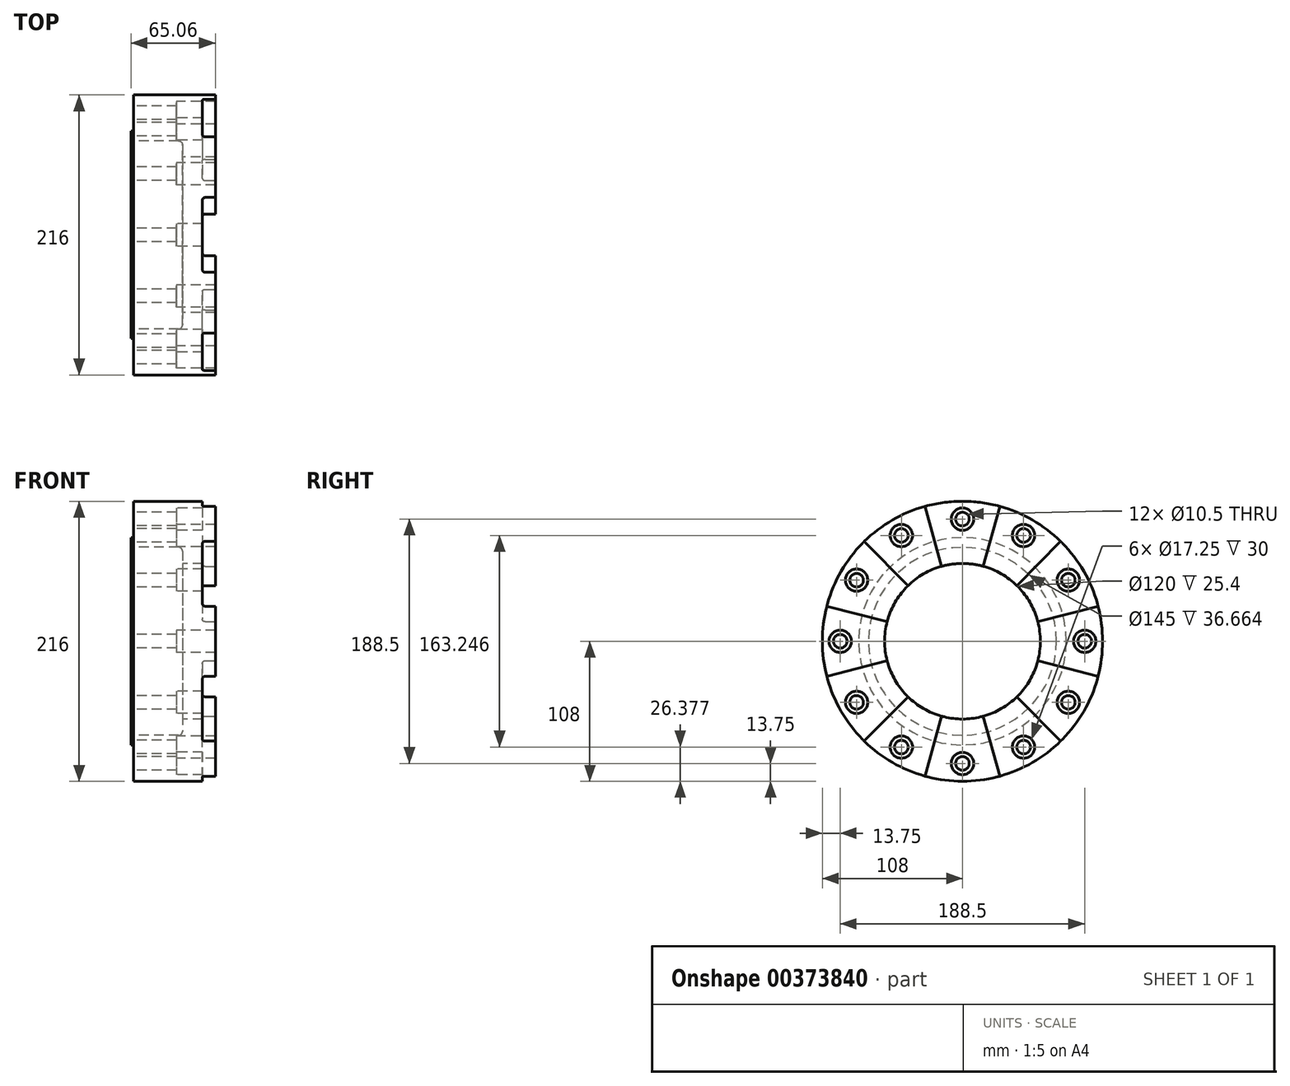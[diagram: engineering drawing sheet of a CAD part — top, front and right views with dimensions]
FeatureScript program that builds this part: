
annotation { "Feature Type Name" : "Feature", "Feature Type Description" : "" }
export const myFeature = defineFeature(function(context is Context, id is Id, definition is map)
    precondition{}
    {
        {
            var Q0;
            Q0=qCreatedBy(makeId("Front.planeOp"),FACE);
            var sketch = newSketch(context, id + "F0", { "sketchPlane" : qUnion([Q0])});
            skLineSegment(sketch, "E0", {"start": v(0, 0) * mm, "end": v(87.54, 0) * mm, "construction": true});
            skLineSegment(sketch, "E1", {"start": v(79.56, 108) * mm, "end": v(79.56, 60) * mm});
            skLineSegment(sketch, "E2", {"start": v(79.56, 60) * mm, "end": v(54.16, 60) * mm});
            skLineSegment(sketch, "E3", {"start": v(54.16, 60) * mm, "end": v(54.16, 69.5) * mm});
            skPoint(sketch, "E4.visualSharp", {"position": v(54.16, 72.5) * mm});
            skLineSegment(sketch, "E5", {"start": v(16.5, 80) * mm, "end": v(16.5, 108) * mm});
            skLineSegment(sketch, "E6", {"start": v(16.5, 108) * mm, "end": v(79.56, 108) * mm});
            skLineSegment(sketch, "E7", {"start": v(14.5, 72.5) * mm, "end": v(14.5, 80) * mm});
            skLineSegment(sketch, "E8", {"start": v(14.5, 80) * mm, "end": v(16.5, 80) * mm});
            skLineSegment(sketch, "E9", {"start": v(14.5, 72.5) * mm, "end": v(51.16, 72.5) * mm});
            skArc(sketch, "E10.filletArc", {"start": v(54.16, 69.5) * mm, "mid": v(53.29, 71.62) * mm, "end": v(51.16, 72.5) * mm});
            skSolve(sketch);
        }
        {
            var Q0;
            Q0=qSketchRegion(id+"F0",true);
            var Q1;
            Q1=sQuery(id+"F0.wireOp",EDGE,"E0");
            revolve(context, id + "F1", {"entities" : qUnion([Q0]), "axis" : qUnion([Q1]), "revolveType" : RevolveType.FULL});
        }
        {
            var Q0;
            Q0=makeQuery(id+"F1.opRevolve","SWEPT_FACE",FACE,{"disambiguationData":[OSD([sQuery(id+"F0.wireOp",EDGE,"E1")])]});
            var sketch = newSketch(context, id + "F2", { "sketchPlane" : qUnion([Q0])});
            skLineSegment(sketch, "E11", {"start": v(0, 0) * mm, "end": v(0, 110.4) * mm, "construction": true});
            skArc(sketch, "E12", {"start": v(-16.03, 57.82) * mm, "mid": v(0, 60) * mm, "end": v(16.03, 57.82) * mm});
            skArc(sketch, "E13", {"start": v(-28.86, 104.07) * mm, "mid": v(0, 108) * mm, "end": v(28.86, 104.07) * mm});
            skLineSegment(sketch, "E14", {"start": v(-28.86, 104.07) * mm, "end": v(-16.03, 57.82) * mm});
            skLineSegment(sketch, "E15", {"start": v(28.86, 104.07) * mm, "end": v(16.03, 57.82) * mm});
            skLineSegment(sketch, "E16.1.0", {"start": v(-75.7, 77.03) * mm, "end": v(-42.05, 42.8) * mm});
            skArc(sketch, "E16.1.1", {"start": v(-58.09, 15.02) * mm, "mid": v(-51.96, 30) * mm, "end": v(-42.05, 42.8) * mm});
            skArc(sketch, "E16.1.2", {"start": v(-104.56, 27.04) * mm, "mid": v(-93.53, 54) * mm, "end": v(-75.7, 77.03) * mm});
            skLineSegment(sketch, "E16.1.3", {"start": v(-104.56, 27.04) * mm, "end": v(-58.09, 15.02) * mm});
            skLineSegment(sketch, "E16.2.0", {"start": v(-104.56, -27.04) * mm, "end": v(-58.09, -15.02) * mm});
            skArc(sketch, "E16.2.1", {"start": v(-42.05, -42.8) * mm, "mid": v(-51.96, -30) * mm, "end": v(-58.09, -15.02) * mm});
            skArc(sketch, "E16.2.2", {"start": v(-75.7, -77.03) * mm, "mid": v(-93.53, -54) * mm, "end": v(-104.56, -27.04) * mm});
            skLineSegment(sketch, "E16.2.3", {"start": v(-75.7, -77.03) * mm, "end": v(-42.05, -42.8) * mm});
            skLineSegment(sketch, "E16.3.0", {"start": v(-28.86, -104.07) * mm, "end": v(-16.03, -57.82) * mm});
            skArc(sketch, "E16.3.1", {"start": v(16.03, -57.82) * mm, "mid": v(0, -60) * mm, "end": v(-16.03, -57.82) * mm});
            skArc(sketch, "E16.3.2", {"start": v(28.86, -104.07) * mm, "mid": v(0, -108) * mm, "end": v(-28.86, -104.07) * mm});
            skLineSegment(sketch, "E16.3.3", {"start": v(28.86, -104.07) * mm, "end": v(16.03, -57.82) * mm});
            skLineSegment(sketch, "E16.4.0", {"start": v(75.7, -77.03) * mm, "end": v(42.05, -42.8) * mm});
            skArc(sketch, "E16.4.1", {"start": v(58.09, -15.02) * mm, "mid": v(51.96, -30) * mm, "end": v(42.05, -42.8) * mm});
            skArc(sketch, "E16.4.2", {"start": v(104.56, -27.04) * mm, "mid": v(93.53, -54) * mm, "end": v(75.7, -77.03) * mm});
            skLineSegment(sketch, "E16.4.3", {"start": v(104.56, -27.04) * mm, "end": v(58.09, -15.02) * mm});
            skLineSegment(sketch, "E16.5.0", {"start": v(104.56, 27.04) * mm, "end": v(58.09, 15.02) * mm});
            skArc(sketch, "E16.5.1", {"start": v(42.05, 42.8) * mm, "mid": v(51.96, 30) * mm, "end": v(58.09, 15.02) * mm});
            skArc(sketch, "E16.5.2", {"start": v(75.7, 77.03) * mm, "mid": v(93.53, 54) * mm, "end": v(104.56, 27.04) * mm});
            skLineSegment(sketch, "E16.5.3", {"start": v(75.7, 77.03) * mm, "end": v(42.05, 42.8) * mm});
            skSolve(sketch);
        }
        {
            var Q0;
            Q0=qSketchRegion(id+"F2",true);
            extrude(context, id + "F3", {"entities" : qUnion([Q0]), "operationType" : NewBodyOperationType.REMOVE, "oppositeDirection" : true, "depth" : 10 * mm});
        }
        {
            var Q0;
            Q0=makeQuery(id+"F3.boolean.opBoolean","SPLIT",FACE,{"disambiguationData":[TD([makeQuery(id+"F3.opExtrude","SWEPT_FACE",FACE,{"disambiguationData":[OSD([sQuery(id+"F2.wireOp",EDGE,"E14")])]})])],"derivedFrom":makeQuery(id+"F1.opRevolve","SWEPT_FACE",FACE,{"disambiguationData":[OSD([sQuery(id+"F0.wireOp",EDGE,"E1")])]})});
            var sketch = newSketch(context, id + "F4", { "sketchPlane" : qUnion([Q0])});
            skLineSegment(sketch, "E17", {"start": v(0, 0) * mm, "end": v(0, 94.25) * mm, "construction": true});
            skCircle(sketch, "E18", {"center": v(0, 94.25) * mm, "radius": 5 * mm});
            skCircle(sketch, "E19.1.0", {"center": v(-47.12, 81.62) * mm, "radius": 5 * mm});
            skCircle(sketch, "E19.2.0", {"center": v(-81.62, 47.13) * mm, "radius": 5 * mm});
            skCircle(sketch, "E19.3.0", {"center": v(-94.25, 0) * mm, "radius": 5 * mm});
            skCircle(sketch, "E19.4.0", {"center": v(-81.62, -47.12) * mm, "radius": 5 * mm});
            skCircle(sketch, "E19.5.0", {"center": v(-47.13, -81.62) * mm, "radius": 5 * mm});
            skCircle(sketch, "E19.6.0", {"center": v(0, -94.25) * mm, "radius": 5 * mm});
            skCircle(sketch, "E19.7.0", {"center": v(47.12, -81.62) * mm, "radius": 5 * mm});
            skCircle(sketch, "E19.8.0", {"center": v(81.62, -47.13) * mm, "radius": 5 * mm});
            skCircle(sketch, "E19.9.0", {"center": v(94.25, 0) * mm, "radius": 5 * mm});
            skCircle(sketch, "E19.10.0", {"center": v(81.62, 47.12) * mm, "radius": 5 * mm});
            skCircle(sketch, "E19.11.0", {"center": v(47.12, 81.62) * mm, "radius": 5 * mm});
            skPoint(sketch, "E19.center", {"position": v(0, 0) * mm});
            skCircle(sketch, "E20", {"center": v(0, 0) * mm, "radius": 94.25 * mm, "construction": true});
            skSolve(sketch);
        }
        {
            var Q0;
            Q0=sQuery(id+"F4.wireOp",VERTEX,"E19.1.0.center");
            var Q1;
            Q1=sQuery(id+"F4.wireOp",VERTEX,"E19.3.0.center");
            var Q2;
            Q2=sQuery(id+"F4.wireOp",VERTEX,"E19.5.0.center");
            var Q3;
            Q3=sQuery(id+"F4.wireOp",VERTEX,"E19.11.0.center");
            var Q4;
            Q4=sQuery(id+"F4.wireOp",VERTEX,"E19.9.0.center");
            var Q5;
            Q5=sQuery(id+"F4.wireOp",VERTEX,"E19.7.0.center");
            var Q6;
            Q6=makeQuery(id+"F1.opRevolve","SWEPT_BODY",BODY,{"disambiguationData":[OSD([sQuery(id+"F0.wireOp",EDGE,"cKsjdh96-D89g-5p2D-h3XL-UVhXMyCSQNq4"),sQuery(id+"F0.wireOp",EDGE,"apuWihD5-RSD5-dsa5-vE7C-J3piarLAXm6q"),sQuery(id+"F0.wireOp",EDGE,"KV8aVnY1-u6Om-Dk3w-krVR-1GxTJCxTkb02"),sQuery(id+"F0.wireOp",EDGE,"Kmc8ooil-dtvY-6vtC-WxYi-Np3pAdkpifhF"),sQuery(id+"F0.wireOp",EDGE,"9beadaba-26b4-418a-b517-611681b9f9d4.filletArc"),sQuery(id+"F0.wireOp",EDGE,"E1"),sQuery(id+"F0.wireOp",EDGE,"E2"),sQuery(id+"F0.wireOp",EDGE,"E3"),sQuery(id+"F0.wireOp",EDGE,"DEHAbUA3-ssQc-y9Ke-qyxT-0Mpok7RH61FX"),sQuery(id+"F0.wireOp",EDGE,"E4.filletArc")])]});
            hole(context, id + "F5", {"style" : HoleStyle.C_BORE, "endStyle" : HoleEndStyle.THROUGH, "holeDiameter" : 10.5 * mm, "cBoreDiameter" : 17.25 * mm, "cBoreDepth" : 30 * mm, "majorDiameter" : 5 * mm, "tappedDepth" : 12 * mm, "tapClearance" : 3, "locations" : qUnion([Q0, Q1, Q2, Q3, Q4, Q5]), "scope" : qUnion([Q6]), "startStyle" : HoleStartStyle.SKETCH});
        }
        {
            var Q0;
            Q0=makeQuery(id+"F3.boolean.opBoolean","COPY",FACE,{"derivedFrom":makeQuery(id+"F3.opExtrude","CAP_FACE",FACE,{"disambiguationData":[OSD([sQuery(id+"F2.wireOp",EDGE,"E12"),sQuery(id+"F2.wireOp",EDGE,"E13"),sQuery(id+"F2.wireOp",EDGE,"E14"),sQuery(id+"F2.wireOp",EDGE,"E15")])],"isStart":false})});
            var sketch = newSketch(context, id + "F6", { "sketchPlane" : qUnion([Q0])});
            skPoint(sketch, "E21", {"position": v(0, 94.25) * mm});
            skPoint(sketch, "E22.1.0", {"position": v(-81.62, 47.12) * mm});
            skPoint(sketch, "E22.2.0", {"position": v(-81.62, -47.12) * mm});
            skPoint(sketch, "E22.3.0", {"position": v(0, -94.25) * mm});
            skPoint(sketch, "E22.4.0", {"position": v(81.62, -47.13) * mm});
            skPoint(sketch, "E22.5.0", {"position": v(81.62, 47.12) * mm});
            skPoint(sketch, "E22.center", {"position": v(0, 0) * mm});
            skSolve(sketch);
        }
        {
            var Q0;
            Q0=sQuery(id+"F6.wireOp",VERTEX,"E21");
            var Q1;
            Q1=sQuery(id+"F6.wireOp",VERTEX,"E22.1.0");
            var Q2;
            Q2=sQuery(id+"F6.wireOp",VERTEX,"E22.2.0");
            var Q3;
            Q3=sQuery(id+"F6.wireOp",VERTEX,"E22.3.0");
            var Q4;
            Q4=sQuery(id+"F6.wireOp",VERTEX,"E22.4.0");
            var Q5;
            Q5=sQuery(id+"F6.wireOp",VERTEX,"E22.5.0");
            var Q6;
            Q6=makeQuery(id+"F1.opRevolve","SWEPT_BODY",BODY,{"disambiguationData":[OSD([sQuery(id+"F0.wireOp",EDGE,"cKsjdh96-D89g-5p2D-h3XL-UVhXMyCSQNq4"),sQuery(id+"F0.wireOp",EDGE,"apuWihD5-RSD5-dsa5-vE7C-J3piarLAXm6q"),sQuery(id+"F0.wireOp",EDGE,"KV8aVnY1-u6Om-Dk3w-krVR-1GxTJCxTkb02"),sQuery(id+"F0.wireOp",EDGE,"Kmc8ooil-dtvY-6vtC-WxYi-Np3pAdkpifhF"),sQuery(id+"F0.wireOp",EDGE,"9beadaba-26b4-418a-b517-611681b9f9d4.filletArc"),sQuery(id+"F0.wireOp",EDGE,"E1"),sQuery(id+"F0.wireOp",EDGE,"E2"),sQuery(id+"F0.wireOp",EDGE,"E3"),sQuery(id+"F0.wireOp",EDGE,"DEHAbUA3-ssQc-y9Ke-qyxT-0Mpok7RH61FX"),sQuery(id+"F0.wireOp",EDGE,"E4.filletArc")])]});
            hole(context, id + "F7", {"style" : HoleStyle.C_BORE, "endStyle" : HoleEndStyle.THROUGH, "holeDiameter" : 10.5 * mm, "cBoreDiameter" : 17.25 * mm, "cBoreDepth" : 20 * mm, "majorDiameter" : 5 * mm, "tappedDepth" : 12 * mm, "tapClearance" : 3, "locations" : qUnion([Q0, Q1, Q2, Q3, Q4, Q5]), "scope" : qUnion([Q6]), "startStyle" : HoleStartStyle.SKETCH});
        }
        {
            var Q0;
            Q0=makeQuery(id+"F3.boolean.opBoolean","COPY",EDGE,{"derivedFrom":makeQuery(id+"F3.opExtrude","CAP_EDGE",EDGE,{"disambiguationData":[OSD([sQuery(id+"F2.wireOp",EDGE,"E15")])],"isStart":true})});
            var Q1;
            Q1=makeQuery(id+"F3.boolean.opBoolean","COPY",EDGE,{"derivedFrom":makeQuery(id+"F3.opExtrude","CAP_EDGE",EDGE,{"disambiguationData":[OSD([sQuery(id+"F2.wireOp",EDGE,"E15")])],"isStart":false})});
            var Q2;
            Q2=makeQuery(id+"F3.boolean.opBoolean","COPY",EDGE,{"derivedFrom":makeQuery(id+"F3.opExtrude","CAP_EDGE",EDGE,{"disambiguationData":[OSD([sQuery(id+"F2.wireOp",EDGE,"E14")])],"isStart":true})});
            var Q3;
            Q3=makeQuery(id+"F3.boolean.opBoolean","COPY",EDGE,{"derivedFrom":makeQuery(id+"F3.opExtrude","CAP_EDGE",EDGE,{"disambiguationData":[OSD([sQuery(id+"F2.wireOp",EDGE,"E16.1.0")])],"isStart":true})});
            var Q4;
            Q4=makeQuery(id+"F3.boolean.opBoolean","COPY",EDGE,{"derivedFrom":makeQuery(id+"F3.opExtrude","CAP_EDGE",EDGE,{"disambiguationData":[OSD([sQuery(id+"F2.wireOp",EDGE,"E16.1.0")])],"isStart":false})});
            var Q5;
            Q5=makeQuery(id+"F3.boolean.opBoolean","COPY",EDGE,{"derivedFrom":makeQuery(id+"F3.opExtrude","CAP_EDGE",EDGE,{"disambiguationData":[OSD([sQuery(id+"F2.wireOp",EDGE,"E16.1.3")])],"isStart":false})});
            var Q6;
            Q6=makeQuery(id+"F3.boolean.opBoolean","COPY",EDGE,{"derivedFrom":makeQuery(id+"F3.opExtrude","CAP_EDGE",EDGE,{"disambiguationData":[OSD([sQuery(id+"F2.wireOp",EDGE,"E16.1.3")])],"isStart":true})});
            var Q7;
            Q7=makeQuery(id+"F3.boolean.opBoolean","COPY",EDGE,{"derivedFrom":makeQuery(id+"F3.opExtrude","CAP_EDGE",EDGE,{"disambiguationData":[OSD([sQuery(id+"F2.wireOp",EDGE,"E16.2.0")])],"isStart":true})});
            var Q8;
            Q8=makeQuery(id+"F3.boolean.opBoolean","COPY",EDGE,{"derivedFrom":makeQuery(id+"F3.opExtrude","CAP_EDGE",EDGE,{"disambiguationData":[OSD([sQuery(id+"F2.wireOp",EDGE,"E16.2.3")])],"isStart":false})});
            var Q9;
            Q9=makeQuery(id+"F3.boolean.opBoolean","COPY",EDGE,{"derivedFrom":makeQuery(id+"F3.opExtrude","CAP_EDGE",EDGE,{"disambiguationData":[OSD([sQuery(id+"F2.wireOp",EDGE,"E16.2.3")])],"isStart":true})});
            var Q10;
            Q10=makeQuery(id+"F3.boolean.opBoolean","COPY",EDGE,{"derivedFrom":makeQuery(id+"F3.opExtrude","CAP_EDGE",EDGE,{"disambiguationData":[OSD([sQuery(id+"F2.wireOp",EDGE,"E16.3.0")])],"isStart":true})});
            var Q11;
            Q11=makeQuery(id+"F3.boolean.opBoolean","COPY",EDGE,{"derivedFrom":makeQuery(id+"F3.opExtrude","CAP_EDGE",EDGE,{"disambiguationData":[OSD([sQuery(id+"F2.wireOp",EDGE,"E16.3.3")])],"isStart":false})});
            var Q12;
            Q12=makeQuery(id+"F3.boolean.opBoolean","COPY",EDGE,{"derivedFrom":makeQuery(id+"F3.opExtrude","CAP_EDGE",EDGE,{"disambiguationData":[OSD([sQuery(id+"F2.wireOp",EDGE,"E16.3.3")])],"isStart":true})});
            var Q13;
            Q13=makeQuery(id+"F3.boolean.opBoolean","COPY",EDGE,{"derivedFrom":makeQuery(id+"F3.opExtrude","CAP_EDGE",EDGE,{"disambiguationData":[OSD([sQuery(id+"F2.wireOp",EDGE,"E16.4.0")])],"isStart":true})});
            var Q14;
            Q14=makeQuery(id+"F3.boolean.opBoolean","COPY",EDGE,{"derivedFrom":makeQuery(id+"F3.opExtrude","CAP_EDGE",EDGE,{"disambiguationData":[OSD([sQuery(id+"F2.wireOp",EDGE,"E16.4.3")])],"isStart":true})});
            var Q15;
            Q15=makeQuery(id+"F3.boolean.opBoolean","COPY",EDGE,{"derivedFrom":makeQuery(id+"F3.opExtrude","CAP_EDGE",EDGE,{"disambiguationData":[OSD([sQuery(id+"F2.wireOp",EDGE,"E16.5.0")])],"isStart":true})});
            var Q16;
            Q16=makeQuery(id+"F3.boolean.opBoolean","COPY",EDGE,{"derivedFrom":makeQuery(id+"F3.opExtrude","CAP_EDGE",EDGE,{"disambiguationData":[OSD([sQuery(id+"F2.wireOp",EDGE,"E16.5.0")])],"isStart":false})});
            var Q17;
            Q17=makeQuery(id+"F3.boolean.opBoolean","COPY",EDGE,{"derivedFrom":makeQuery(id+"F3.opExtrude","CAP_EDGE",EDGE,{"disambiguationData":[OSD([sQuery(id+"F2.wireOp",EDGE,"E16.5.3")])],"isStart":true})});
            var Q18;
            Q18=makeQuery(id+"F3.boolean.opBoolean","COPY",EDGE,{"derivedFrom":makeQuery(id+"F3.opExtrude","CAP_EDGE",EDGE,{"disambiguationData":[OSD([sQuery(id+"F2.wireOp",EDGE,"E16.5.3")])],"isStart":false})});
            var Q19;
            Q19=makeQuery(id+"F3.boolean.opBoolean","COPY",EDGE,{"derivedFrom":makeQuery(id+"F3.opExtrude","CAP_EDGE",EDGE,{"disambiguationData":[OSD([sQuery(id+"F2.wireOp",EDGE,"E14")])],"isStart":false})});
            var Q20;
            Q20=makeQuery(id+"F3.boolean.opBoolean","COPY",EDGE,{"derivedFrom":makeQuery(id+"F3.opExtrude","CAP_EDGE",EDGE,{"disambiguationData":[OSD([sQuery(id+"F2.wireOp",EDGE,"E16.2.0")])],"isStart":false})});
            var Q21;
            Q21=makeQuery(id+"F3.boolean.opBoolean","COPY",EDGE,{"derivedFrom":makeQuery(id+"F3.opExtrude","CAP_EDGE",EDGE,{"disambiguationData":[OSD([sQuery(id+"F2.wireOp",EDGE,"E16.3.0")])],"isStart":false})});
            var Q22;
            Q22=makeQuery(id+"F3.boolean.opBoolean","COPY",EDGE,{"derivedFrom":makeQuery(id+"F3.opExtrude","CAP_EDGE",EDGE,{"disambiguationData":[OSD([sQuery(id+"F2.wireOp",EDGE,"E16.4.3")])],"isStart":false})});
            var Q23;
            Q23=makeQuery(id+"F3.boolean.opBoolean","COPY",EDGE,{"derivedFrom":makeQuery(id+"F3.opExtrude","CAP_EDGE",EDGE,{"disambiguationData":[OSD([sQuery(id+"F2.wireOp",EDGE,"E16.4.0")])],"isStart":false})});
            fillet(context, id + "F8", {"entities" : qUnion([Q0, Q1, Q2, Q3, Q4, Q5, Q6, Q7, Q8, Q9, Q10, Q11, Q12, Q13, Q14, Q15, Q16, Q17, Q18, Q19, Q20, Q21, Q22, Q23]), "radius" : 2 * mm, "tangentPropagation" : true, "allowEdgeOverflow" : false});
        }
    });
